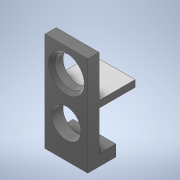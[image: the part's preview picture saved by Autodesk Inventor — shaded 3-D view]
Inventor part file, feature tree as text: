
AUTODESK INVENTOR PART (.ipt)
format: ipt  version: 2022 (Build 260153000, 153)  size: 154,112 bytes
history: native  units: mm
features: extrude x4, sketch x3, other x1, chamfer x1
ambient origin geometry x8: Origin, YZ Plane, XZ Plane, XY Plane, X Axis, Y Axis, Z Axis, Center Point
bodies: Body1 (feature_tree)
feature tree (9):
  other  "ソリッド1"
  extrude  "スペーサ"  Depth=7.6mm
  sketch  "スケッチ2"
  extrude  "押し出し2"  TaperAngle=0.0deg  [1 undecoded]
  extrude  "押し出し5"  Depth=5.8mm
  chamfer  "面取り1"  Distance=2.0mm
  extrude  "足"  Depth=1.2mm
  sketch  "スケッチ1"
  sketch  "スケッチ4"
note: 1 required parameter value undecoded (feature->parameter linkage not recoverable at this tier; creation-order binding heuristic only, values carry confidence <= 0.55)
